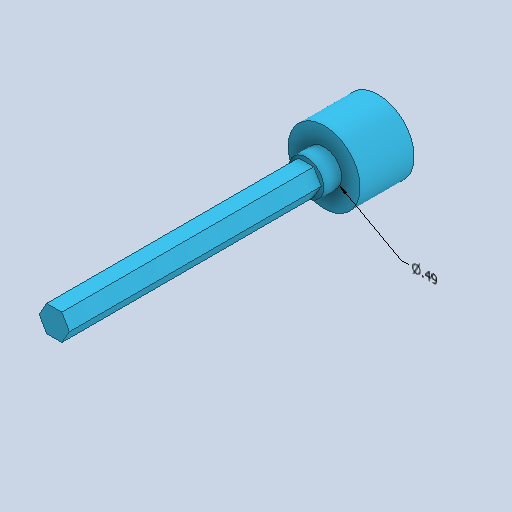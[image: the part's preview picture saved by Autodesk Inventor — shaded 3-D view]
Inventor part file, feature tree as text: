
AUTODESK INVENTOR PART (.ipt)
format: ipt  version: 2022.2 (Build 262287030, 287C)  size: 143,872 bytes
history: native  units: in
note: dims shown in document units (in); Inventor stores cm internally (conversion verified against a paired STEP export)
features: other x4, extrude x3, sketch x3
ambient origin geometry x8: Origin, YZ Plane, XZ Plane, XY Plane, X Axis, Y Axis, Z Axis, Center Point
bodies: Body1 (feature_tree)
feature tree (10):
  other  "Annotations"
  extrude  "Extrusion2"  Depth=4.5in TaperAngle=0.0deg
  extrude  "Extrusion4"  Depth=1.0in
  other  "Reduce Hex Shaft"
  extrude  "Extrusion5"  Depth=0.25in
  other  "Reduce Base Bushing"
  sketch  "Sketch1"  dims[d0=0.375in d4=4.5in d5=0.0in]
  sketch  "Sketch4"  dims[d6=0.001in d10=1.0in]
  sketch  "Sketch5"  dims[d11=0.75in d12=0.0in d13=0.005in d14=0.005in d15=0.5in d16=0.25in d17=0.0in d20=0.005in d21=0.005in d23=2.2764in d24=0.49in]
  other  "Diameter Dimension 1"
